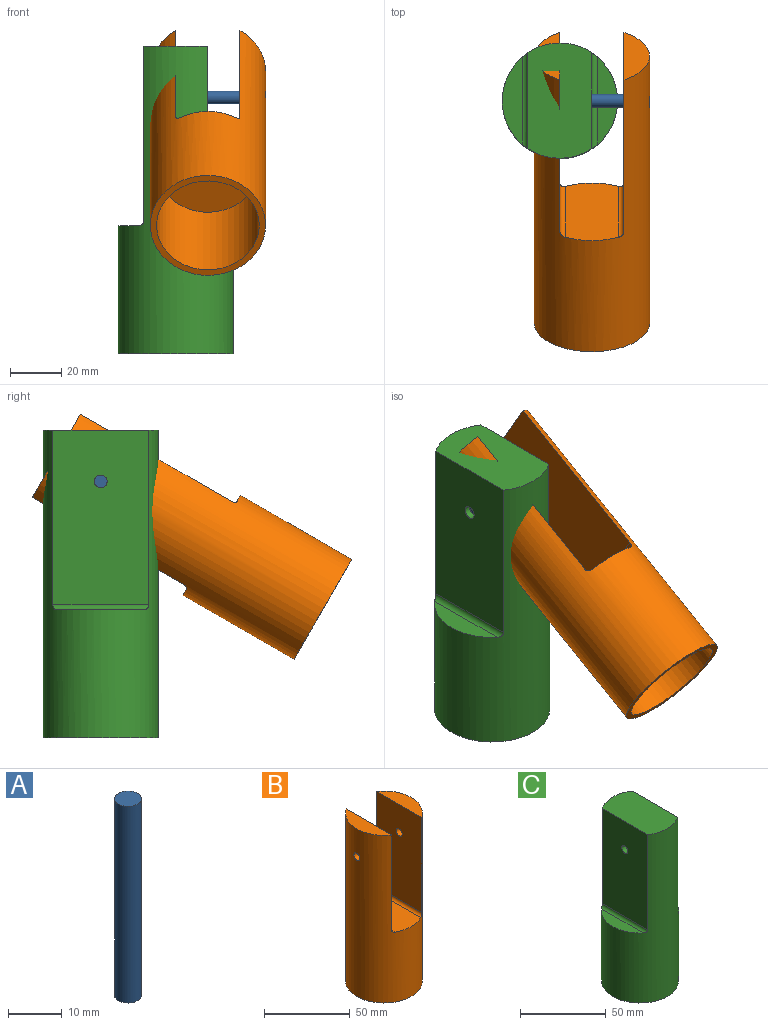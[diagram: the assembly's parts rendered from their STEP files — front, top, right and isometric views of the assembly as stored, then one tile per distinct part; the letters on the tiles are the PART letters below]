
ASSEMBLY  parts=3 mates=2
PART A: 3 faces, bbox 5x5x45 mm
  f0: cylinder r=2.5mm len=45mm, axis (0,0,-1), area 706.9mm2, adj f1,f2
  f1: plane 5x5mm, normal (0,0,1), area 19.6mm2, adj f0
  f2: plane 5x5mm, normal (0,0,-1), area 19.6mm2, adj f0
PART B: 13 faces, bbox 45x45x120 mm
  f0: cylinder r=22.5mm len=120mm, axis (0,0,-1), area 13218.5mm2, adj f1,f2,f3,f4,f5,f6,f9,f10
  f1: plane 37.42x10mm, normal (0,0,1), area 263.2mm2, adj f0,f5
  f2: plane 37.42x10mm, normal (0,0,1), area 263.2mm2, adj f0,f4
  f3: plane 45x45mm, normal (0,0,-1), area 333.8mm2, adj f0,f7
  f4: plane 68x37.42mm, normal (1,0,0), area 2524.7mm2, adj f0,f2,f10,f11
  f5: plane 68x37.42mm, normal (-1,0,0), area 2524.7mm2, adj f0,f1,f9,f12
  f6: plane 45x21mm, normal (0,0,1), area 909.5mm2, adj f0,f11,f12
  f7: cylinder r=20mm len=45mm, axis (0,0,-1), area 5654.9mm2, adj f3,f8
  f8: plane 40x40mm, normal (0,0,-1), area 1256.6mm2, adj f7
  f9: cylinder r=2.5mm len=10mm, axis (1,0,0), area 156mm2, adj f0,f5
  f10: cylinder r=2.5mm len=10mm, axis (1,0,0), area 156mm2, adj f0,f4
  f11: cylinder r=2mm len=39.8mm, axis (0,-1,0), area 120.4mm2, adj f0,f4,f6
  f12: cylinder r=2mm len=39.8mm, axis (0,1,0), area 120.4mm2, adj f0,f5,f6
PART C: 12 faces, bbox 45x45x120 mm
  f0: plane 45x25mm, normal (0,0,1), area 1064.1mm2, adj f1,f3,f5
  f1: cylinder r=22.5mm len=120mm, axis (0,0,-1), area 10783.7mm2, adj f0,f2,f3,f4,f5,f6,f10,f11
  f2: plane 45x45mm, normal (0,0,-1), area 333.8mm2, adj f1,f7
  f3: plane 68x37.42mm, normal (1,0,0), area 2524.7mm2, adj f0,f1,f9,f10
  f4: plane 34.41x8mm, normal (0,0,1), area 191.2mm2, adj f1,f10
  f5: plane 68x37.42mm, normal (-1,0,0), area 2524.7mm2, adj f0,f1,f9,f11
  f6: plane 34.41x8mm, normal (0,0,1), area 191.2mm2, adj f1,f11
  f7: cylinder r=20mm len=45mm, axis (0,0,-1), area 5654.9mm2, adj f2,f8
  f8: plane 40x40mm, normal (0,0,-1), area 1256.6mm2, adj f7
  f9: cylinder r=2.5mm len=25mm, axis (1,0,0), area 392.7mm2, adj f3,f5
  f10: cylinder r=2mm len=37.42mm, axis (0,-1,0), area 114.3mm2, adj f1,f3,f4
  f11: cylinder r=2mm len=37.42mm, axis (0,1,0), area 114.3mm2, adj f1,f5,f6
PLACE A rot(axis=(-0.45,-0.77,0.45),104.5deg) t=(36.8,153.52,99.95)mm
PLACE B rot(axis=(-1,0,0),60deg) t=(14.24,66.88,50.02)mm
PLACE C t=(1.74,153.52,-0.05)mm fixed
MATE revolute C.f9 <-> B.f9  axis (1,0,0) through (1.74,153.52,99.95)mm
MATE fastened B.f9 <-> A.f0  axis (1,0,0) through (36.8,153.52,99.95)mm
